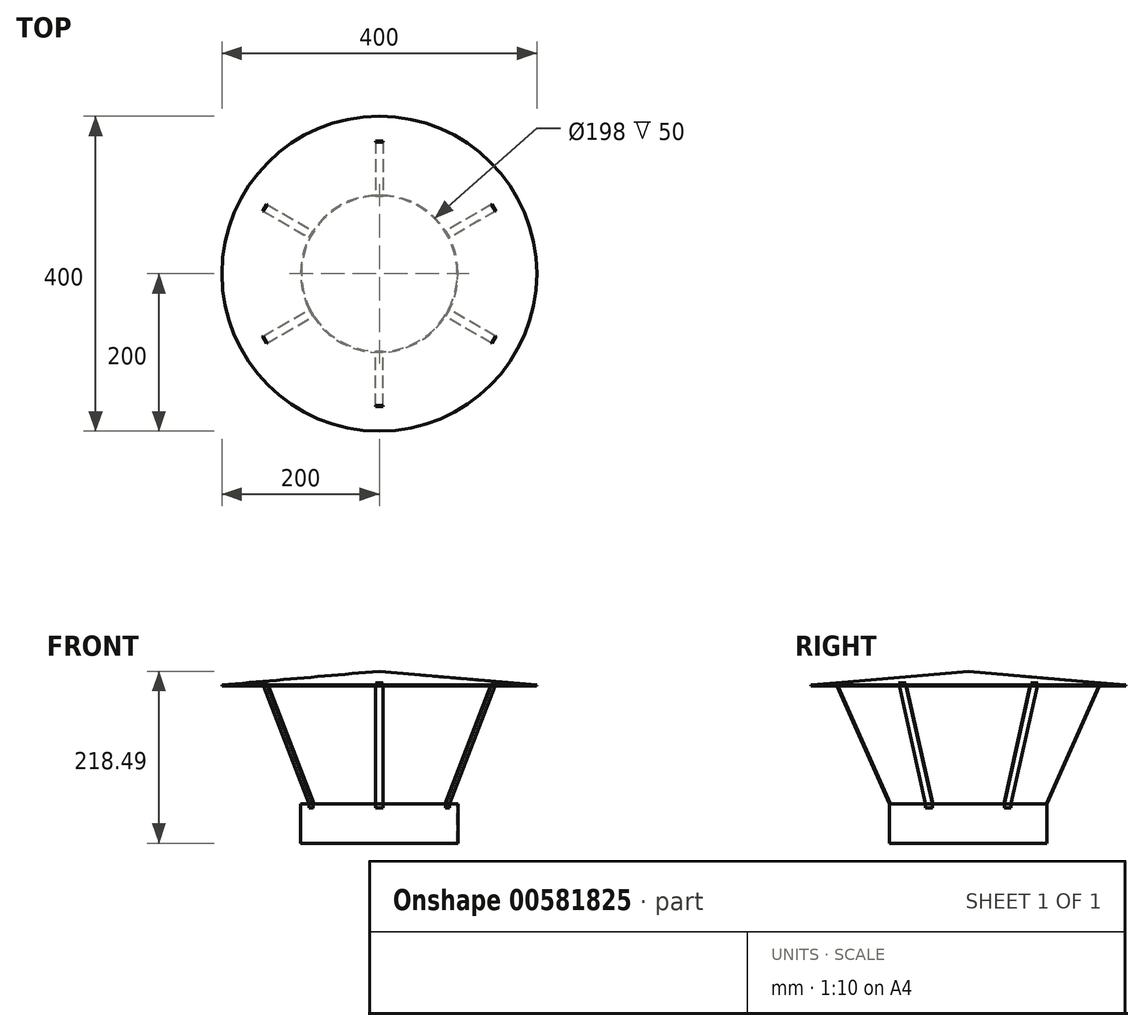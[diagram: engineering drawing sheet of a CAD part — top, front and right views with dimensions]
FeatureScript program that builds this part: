
annotation { "Feature Type Name" : "Feature", "Feature Type Description" : "" }
export const myFeature = defineFeature(function(context is Context, id is Id, definition is map)
    precondition{}
    {
        {
            var Q0;
            Q0=qCreatedBy(makeId("Top.planeOp"),FACE);
            var sketch = newSketch(context, id + "F0", { "sketchPlane" : qUnion([Q0])});
            skCircle(sketch, "E0", {"center": v(0, 0) * mm, "radius": 99 * mm});
            skCircle(sketch, "E1", {"center": v(0, 0) * mm, "radius": 100 * mm});
            skSolve(sketch);
        }
        {
            var Q0;
            Q0=qSketchRegion(id+"F0",true);
            extrude(context, id + "F1", {"entities" : qUnion([Q0]), "oppositeDirection" : true, "depth" : 50 * mm, "offsetDistance" : 25 * mm});
        }
        {
            var Q0;
            Q0=qCreatedBy(makeId("Right.planeOp"),FACE);
            var sketch = newSketch(context, id + "F2", { "sketchPlane" : qUnion([Q0])});
            skLineSegment(sketch, "E2", {"start": v(0, 0) * mm, "end": v(0, 168.5) * mm, "construction": true});
            skLineSegment(sketch, "E3", {"start": v(0, 168.5) * mm, "end": v(-200, 151) * mm});
            skLineSegment(sketch, "E4", {"start": v(-200, 151) * mm, "end": v(-199.91, 150) * mm});
            skLineSegment(sketch, "E5", {"start": v(-199.91, 150) * mm, "end": v(0, 167.5) * mm});
            skLineSegment(sketch, "E6", {"start": v(0, 167.5) * mm, "end": v(0, 168.5) * mm});
            skSolve(sketch);
        }
        {
            var Q0;
            Q0=qSketchRegion(id+"F2",true);
            var Q1;
            Q1=sQuery(id+"F2.wireOp",EDGE,"E2");
            revolve(context, id + "F3", {"surfaceOperationType" : NewSurfaceOperationType.NEW, "entities" : qUnion([Q0]), "axis" : qUnion([Q1]), "revolveType" : RevolveType.FULL});
        }
        {
            var Q0;
            Q0=qCreatedBy(makeId("Right.planeOp"),FACE);
            var sketch = newSketch(context, id + "F4", { "sketchPlane" : qUnion([Q0])});
            skLineSegment(sketch, "E7.0", {"start": v(-100, 0) * mm, "end": v(100, 0) * mm, "construction": true});
            skLineSegment(sketch, "E8", {"start": v(-100, -50) * mm, "end": v(-100, 0) * mm, "construction": true});
            skLineSegment(sketch, "E9", {"start": v(-299.24, 142.31) * mm, "end": v(0.76, 168.56) * mm, "construction": true});
            skLineSegment(sketch, "E10", {"start": v(-167.36, 153.85) * mm, "end": v(-168.41, 153.76) * mm});
            skLineSegment(sketch, "E11", {"start": v(-167.36, 153.85) * mm, "end": v(-98.9, 0) * mm});
            skLineSegment(sketch, "E12", {"start": v(-168.41, 153.76) * mm, "end": v(-100, 0) * mm});
            skLineSegment(sketch, "E13", {"start": v(-198.41, 132.87) * mm, "end": v(-199.91, 150) * mm, "construction": true});
            skLineSegment(sketch, "E14", {"start": v(-100, 0) * mm, "end": v(-100, -5) * mm});
            skLineSegment(sketch, "E15", {"start": v(-100, -5) * mm, "end": v(-98.9, -5) * mm});
            skLineSegment(sketch, "E16", {"start": v(-98.9, -5) * mm, "end": v(-98.9, 0) * mm});
            skSolve(sketch);
        }
        {
            var Q0;
            Q0=qSketchRegion(id+"F4",true);
            extrude(context, id + "F5", {"entities" : qUnion([Q0]), "depth" : 10 * mm, "offsetDistance" : 25 * mm, "symmetric" : true});
        }
        {
            var Q0;
            Q0=qCreatedBy(makeId("Right.planeOp"),FACE);
            var sketch = newSketch(context, id + "F6", { "sketchPlane" : qUnion([Q0])});
            skLineSegment(sketch, "E17", {"start": v(0, 0) * mm, "end": v(0, 275.74) * mm, "construction": true});
            skSolve(sketch);
        }
        {
            var Q0;
            Q0=makeQuery(id+"F5.opExtrude","SWEPT_BODY",BODY,{"disambiguationData":[OSD([sQuery(id+"F4.wireOp",EDGE,"sHu2Gir7-9ggc-A0BL-dRGA-Pvlho7gEY1Av"),sQuery(id+"F4.wireOp",EDGE,"E10"),sQuery(id+"F4.wireOp",EDGE,"E11"),sQuery(id+"F4.wireOp",EDGE,"4oHM4HFf-rFhq-OT9C-b5np-XKB4EdHShkcs"),sQuery(id+"F4.wireOp",EDGE,"343eP1Ns-5I6F-shWL-LBzT-Atdx6hGGUzft"),sQuery(id+"F4.wireOp",EDGE,"I0gdIfue-qcDF-GefX-ffwp-bMTbIkreWT4E")])]});
            var Q1;
            Q1=sQuery(id+"F6.wireOp",EDGE,"E17");
            circularPattern(context, id + "F7", {"entities" : qUnion([Q0]), "axis" : qUnion([Q1]), "angle" : 360 * degree, "instanceCount" : 6, "equalSpace" : true, "computeTransformsWithoutBuiltin" : true});
        }
    });
